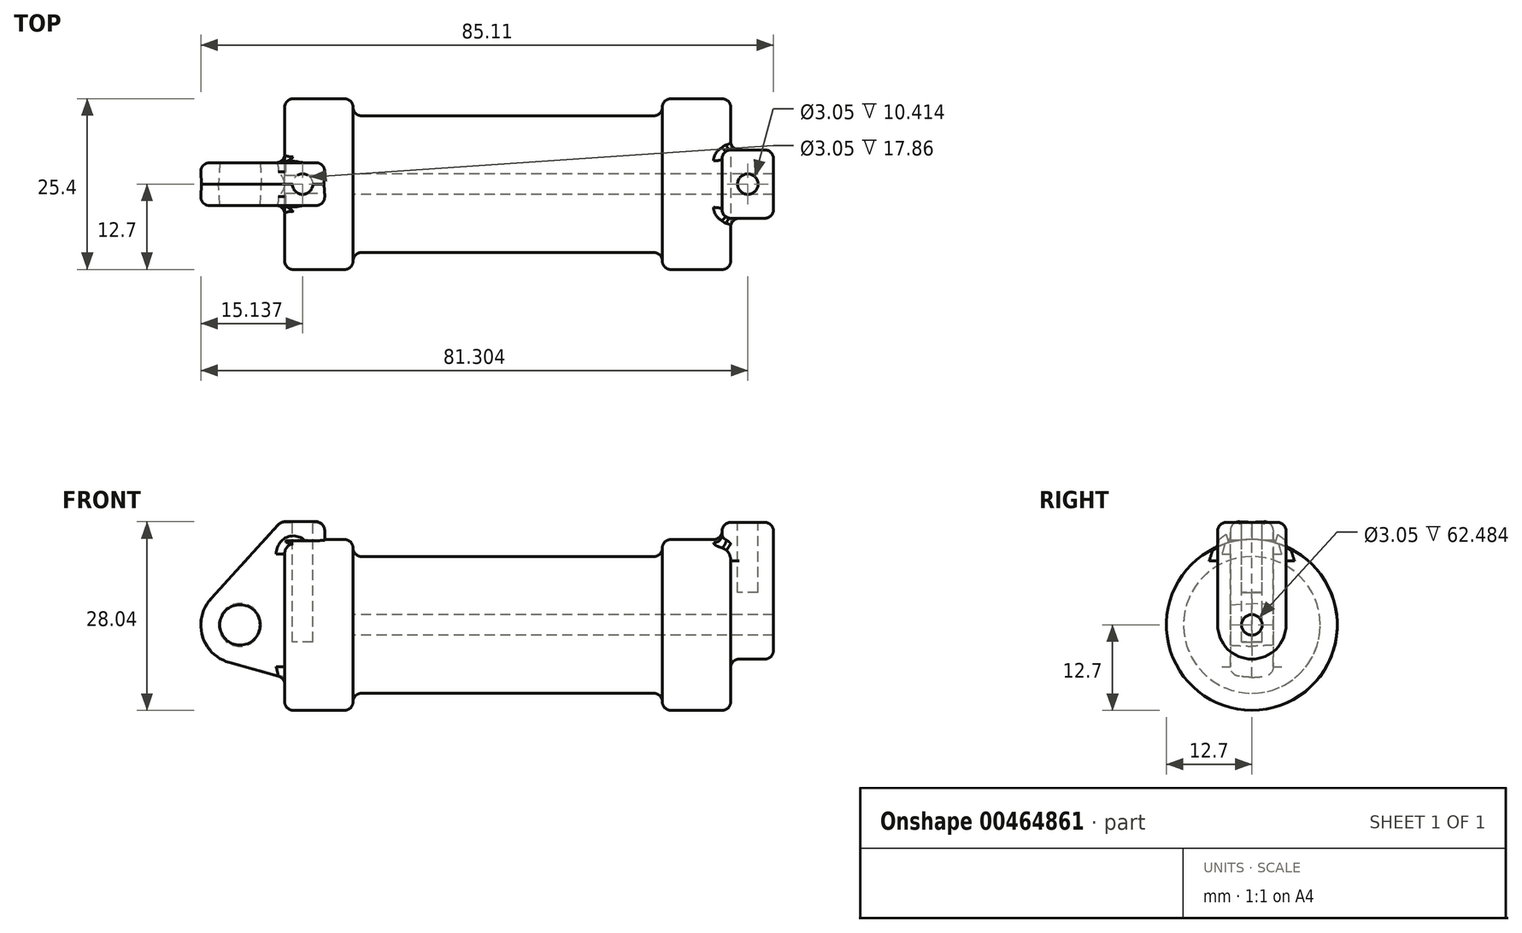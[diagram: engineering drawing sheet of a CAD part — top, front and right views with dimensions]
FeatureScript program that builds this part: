
annotation { "Feature Type Name" : "Feature", "Feature Type Description" : "" }
export const myFeature = defineFeature(function(context is Context, id is Id, definition is map)
    precondition{}
    {
        {
            var Q0;
            Q0=qCreatedBy(makeId("Front.planeOp"),FACE);
            var sketch = newSketch(context, id + "F0", { "sketchPlane" : qUnion([Q0])});
            skLineSegment(sketch, "E0", {"start": v(0, 0) * mm, "end": v(0, 12.7) * mm});
            skLineSegment(sketch, "E1", {"start": v(0, 12.7) * mm, "end": v(10.16, 12.7) * mm});
            skLineSegment(sketch, "E2", {"start": v(10.16, 12.7) * mm, "end": v(10.16, 10.16) * mm});
            skLineSegment(sketch, "E3", {"start": v(10.16, 10.16) * mm, "end": v(56.13, 10.16) * mm});
            skLineSegment(sketch, "E4", {"start": v(56.13, 10.16) * mm, "end": v(56.13, 12.7) * mm});
            skLineSegment(sketch, "E5", {"start": v(56.13, 12.7) * mm, "end": v(66.3, 12.7) * mm});
            skLineSegment(sketch, "E6", {"start": v(66.3, 12.7) * mm, "end": v(66.3, 0) * mm});
            skLineSegment(sketch, "E7", {"start": v(66.3, 0) * mm, "end": v(0, 0) * mm});
            skLineSegment(sketch, "E8", {"start": v(5.84, 15.24) * mm, "end": v(-0.5, 15.24) * mm});
            skLineSegment(sketch, "E9", {"start": v(-0.5, 15.24) * mm, "end": v(-10.88, 3.85) * mm});
            skLineSegment(sketch, "E10", {"start": v(0, 0) * mm, "end": v(-6.65, 0) * mm});
            skCircle(sketch, "E11", {"center": v(-6.65, 0) * mm, "radius": 5.72 * mm});
            skCircle(sketch, "E12", {"center": v(-6.65, 0) * mm, "radius": 3.18 * mm});
            skLineSegment(sketch, "E13", {"start": v(5.84, 15.24) * mm, "end": v(5.84, -9.4) * mm});
            skLineSegment(sketch, "E14", {"start": v(5.84, -9.4) * mm, "end": v(-8.18, -5.5) * mm});
            skLineSegment(sketch, "E15", {"start": v(0, 0) * mm, "end": v(0, -7.78) * mm});
            skSolve(sketch);
        }
        {
            var Q0;
            {var subQ0=sQuery(id+"F0.wireOp",EDGE,"E2");Q0=makeQuery(id+"F0.imprint","IMPRINT",FACE,{"disambiguationData":[TD([[makeQuery(id+"F0.imprint","IMPRINT",EDGE,{"derivedFrom":subQ0}),-1.0]])]});}
            var Q1;
            {var subQ0=sQuery(id+"F0.wireOp",EDGE,"E0");Q1=makeQuery(id+"F0.imprint","IMPRINT",FACE,{"disambiguationData":[TD([[makeQuery(id+"F0.imprint","IMPRINT",EDGE,{"derivedFrom":subQ0}),-1.0]])]});}
            var Q2;
            Q2=sQuery(id+"F0.wireOp",EDGE,"E7");
            revolve(context, id + "F1", {"entities" : qUnion([Q0, Q1]), "axis" : qUnion([Q2]), "revolveType" : RevolveType.FULL});
        }
        {
            var Q0;
            {var subQ1=sQuery(id+"F0.wireOp",EDGE,"E0");Q0=makeQuery(id+"F0.imprint","IMPRINT",FACE,{"disambiguationData":[TD([[makeQuery(id+"F0.imprint","IMPRINT",EDGE,{"derivedFrom":subQ1}),1.0]])]});}
            var Q1;
            {var subQ5=sQuery(id+"F0.wireOp",EDGE,"E12");Q1=makeQuery(id+"F0.imprint","IMPRINT",FACE,{"disambiguationData":[TD([[makeQuery(id+"F0.imprint","IMPRINT",EDGE,{"derivedFrom":subQ5}),-1.0]])]});}
            var Q2;
            {var subQ0=sQuery(id+"F0.wireOp",EDGE,"E15");Q2=makeQuery(id+"F0.imprint","IMPRINT",FACE,{"disambiguationData":[TD([[makeQuery(id+"F0.imprint","IMPRINT",EDGE,{"derivedFrom":subQ0}),-1.0]])]});}
            extrude(context, id + "F2", {"entities" : qUnion([Q0, Q1, Q2]), "operationType" : NewBodyOperationType.ADD, "endBound" : BoundingType.SYMMETRIC, "depth" : 6.35 * mm, "hasDraft" : true, "draftAngle" : 3 * degree});
        }
        {
            var Q0;
            Q0=makeQuery(id+"F1.opRevolve","SWEPT_FACE",FACE,{"disambiguationData":[OSD([sQuery(id+"F0.wireOp",EDGE,"E6")])]});
            var sketch = newSketch(context, id + "F3", { "sketchPlane" : qUnion([Q0])});
            skCircle(sketch, "E16", {"center": v(0, 0) * mm, "radius": 1.52 * mm});
            skCircle(sketch, "E17", {"center": v(0, 0) * mm, "radius": 5.08 * mm});
            skLineSegment(sketch, "E18", {"start": v(-5.08, 0) * mm, "end": v(-5.08, 15.24) * mm});
            skLineSegment(sketch, "E19", {"start": v(-5.08, 15.24) * mm, "end": v(5.08, 15.24) * mm});
            skLineSegment(sketch, "E20", {"start": v(5.08, 15.24) * mm, "end": v(5.08, 0) * mm});
            skSolve(sketch);
        }
        {
            var Q0;
            Q0 = qSketchRegion(id + "F3", true);
            extrude(context, id + "F4", {"entities" : qUnion([Q0]), "operationType" : NewBodyOperationType.ADD, "depth" : 6.35 * mm});
        }
        {
            var Q0;
            Q0 = qSketchRegion(id + "F3", true);
            extrude(context, id + "F5", {"entities" : qUnion([Q0]), "operationType" : NewBodyOperationType.ADD, "oppositeDirection" : true, "depth" : 1.27 * mm});
        }
        {
            var Q0;
            Q0=makeQuery(id+"F4.boolean.opBoolean","SPLIT",FACE,{"disambiguationData":[TD([makeQuery(id+"F4.opExtrude","SWEPT_FACE",FACE,{"disambiguationData":[OSD([sQuery(id+"F3.wireOp",EDGE,"E16")])]})])],"derivedFrom":makeQuery(id+"F1.opRevolve","SWEPT_FACE",FACE,{"disambiguationData":[OSD([sQuery(id+"F0.wireOp",EDGE,"E6")])]})});
            var Q1;
            Q1=makeQuery(id+"F1.opRevolve","SWEPT_FACE",FACE,{"disambiguationData":[OSD([sQuery(id+"F0.wireOp",EDGE,"E2")])]});
            extrude(context, id + "F6", {"entities" : qUnion([Q0]), "operationType" : NewBodyOperationType.REMOVE, "endBound" : BoundingType.UP_TO_SURFACE, "oppositeDirection" : true, "endBoundEntityFace" : qUnion([Q1]), "depth" : 25.4 * mm});
        }
        {
            var Q0;
            {var subQ0=sQuery(id+"F3.wireOp",EDGE,"E19");Q0=makeQuery(id+"F5.boolean.opBoolean","MERGE",FACE,{"derivedFrom":[makeQuery(id+"F4.opExtrude","SWEPT_FACE",FACE,{"disambiguationData":[OSD([subQ0])]}),makeQuery(id+"F5.opExtrude","SWEPT_FACE",FACE,{"disambiguationData":[OSD([subQ0])]})]});}
            var sketch = newSketch(context, id + "F7", { "sketchPlane" : qUnion([Q0])});
            skCircle(sketch, "E21", {"center": v(68.83, 0) * mm, "radius": 1.52 * mm});
            skPoint(sketch, "E22.endSnap0", {"position": v(65.02, 0) * mm});
            skSolve(sketch);
        }
        {
            var Q0;
            Q0 = qSketchRegion(id + "F7", true);
            extrude(context, id + "F8", {"entities" : qUnion([Q0]), "operationType" : NewBodyOperationType.REMOVE, "oppositeDirection" : true, "depth" : 10.4 * mm});
        }
        {
            var Q0;
            {var subQ0=sQuery(id+"F3.wireOp",EDGE,"E19");Q0=makeQuery(id+"F5.boolean.opBoolean","MERGE",FACE,{"derivedFrom":[makeQuery(id+"F4.opExtrude","SWEPT_FACE",FACE,{"disambiguationData":[OSD([subQ0])]}),makeQuery(id+"F5.opExtrude","SWEPT_FACE",FACE,{"disambiguationData":[OSD([subQ0])]})]});}
            var sketch = newSketch(context, id + "F9", { "sketchPlane" : qUnion([Q0])});
            skLineSegment(sketch, "E23.0", {"start": v(5.84, 0) * mm, "end": v(-0.5, 0) * mm});
            skCircle(sketch, "E24", {"center": v(2.67, 0) * mm, "radius": 1.52 * mm});
            skSolve(sketch);
        }
        {
            var Q0;
            Q0 = qSketchRegion(id + "F9", true);
            extrude(context, id + "F10", {"entities" : qUnion([Q0]), "operationType" : NewBodyOperationType.REMOVE, "oppositeDirection" : true, "depth" : 17.78 * mm, "hasSecondDirection" : true, "secondDirectionOppositeDirection" : false, "secondDirectionDepth" : 25.4 * mm});
        }
        {
            var Q0;
            Q0=makeQuery(id+"F1.opRevolve","SWEPT_EDGE",EDGE,{"disambiguationData":[OSD([sQuery(id+"F0.wireOp",EDGE,"E0"),sQuery(id+"F0.wireOp",EDGE,"E1")])]});
            var Q1;
            Q1=makeQuery(id+"F1.opRevolve","SWEPT_EDGE",EDGE,{"disambiguationData":[OSD([sQuery(id+"F0.wireOp",EDGE,"E1"),sQuery(id+"F0.wireOp",EDGE,"E2")])]});
            var Q2;
            Q2=makeQuery(id+"F1.opRevolve","SWEPT_EDGE",EDGE,{"disambiguationData":[OSD([sQuery(id+"F0.wireOp",EDGE,"E2"),sQuery(id+"F0.wireOp",EDGE,"E3")])]});
            var Q3;
            Q3=makeQuery(id+"F1.opRevolve","SWEPT_EDGE",EDGE,{"disambiguationData":[OSD([sQuery(id+"F0.wireOp",EDGE,"E4"),sQuery(id+"F0.wireOp",EDGE,"E5")])]});
            var Q4;
            Q4=makeQuery(id+"F1.opRevolve","SWEPT_EDGE",EDGE,{"disambiguationData":[OSD([sQuery(id+"F0.wireOp",EDGE,"E3"),sQuery(id+"F0.wireOp",EDGE,"E4")])]});
            var Q5;
            {var subQ0=sQuery(id+"F0.wireOp",EDGE,"E5");var subQ1=sQuery(id+"F0.wireOp",EDGE,"E6");Q5=makeQuery(id+"F4.boolean.opBoolean","SPLIT",EDGE,{"disambiguationData":[topologyDisambiguationEdgeConnected([makeQuery(id+"F1.opRevolve","SWEPT_FACE",FACE,{"disambiguationData":[OSD([subQ1])]})])],"derivedFrom":makeQuery(id+"F1.opRevolve","SWEPT_EDGE",EDGE,{"disambiguationData":[OSD([subQ0,subQ1])]})});}
            fillet(context, id + "F11", {"entities" : qUnion([Q0, Q1, Q2, Q3, Q4, Q5]), "radius" : 1.27 * mm, "tangentPropagation" : true, "allowEdgeOverflow" : false});
        }
        {
            var Q0;
            Q0=makeQuery(id+"F4.opExtrude","CAP_EDGE",EDGE,{"disambiguationData":[OSD([sQuery(id+"F3.wireOp",EDGE,"E19")])],"isStart":false});
            var Q1;
            Q1=makeQuery(id+"F4.opExtrude","CAP_EDGE",EDGE,{"disambiguationData":[OSD([sQuery(id+"F3.wireOp",EDGE,"E18")])],"isStart":false});
            var Q2;
            Q2=makeQuery(id+"F4.opExtrude","CAP_EDGE",EDGE,{"disambiguationData":[OSD([sQuery(id+"F3.wireOp",EDGE,"E17")])],"isStart":false});
            var Q3;
            Q3=makeQuery(id+"F4.opExtrude","CAP_EDGE",EDGE,{"disambiguationData":[OSD([sQuery(id+"F3.wireOp",EDGE,"E20")])],"isStart":false});
            var Q4;
            {var subQ0=sQuery(id+"F3.wireOp",EDGE,"E20");var subQ1=sQuery(id+"F3.wireOp",EDGE,"E19");Q4=makeQuery(id+"F5.boolean.opBoolean","MERGE",EDGE,{"derivedFrom":[makeQuery(id+"F4.opExtrude","SWEPT_EDGE",EDGE,{"disambiguationData":[OSD([subQ1,subQ0])]}),makeQuery(id+"F5.opExtrude","SWEPT_EDGE",EDGE,{"disambiguationData":[OSD([subQ1,subQ0])]})]});}
            var Q5;
            {var subQ0=sQuery(id+"F3.wireOp",EDGE,"E19");var subQ1=sQuery(id+"F3.wireOp",EDGE,"E18");Q5=makeQuery(id+"F5.boolean.opBoolean","MERGE",EDGE,{"derivedFrom":[makeQuery(id+"F4.opExtrude","SWEPT_EDGE",EDGE,{"disambiguationData":[OSD([subQ1,subQ0])]}),makeQuery(id+"F5.opExtrude","SWEPT_EDGE",EDGE,{"disambiguationData":[OSD([subQ1,subQ0])]})]});}
            var Q6;
            Q6=makeQuery(id+"F5.opExtrude","CAP_EDGE",EDGE,{"disambiguationData":[OSD([sQuery(id+"F3.wireOp",EDGE,"E19")])],"isStart":false});
            var Q7;
            Q7=makeQuery(id+"F5.boolean.opBoolean","INTERSECT",EDGE,{"derivedFrom":[makeQuery(id+"F1.opRevolve","SWEPT_FACE",FACE,{"disambiguationData":[OSD([sQuery(id+"F0.wireOp",EDGE,"E5")])]}),makeQuery(id+"F5.opExtrude","CAP_FACE",FACE,{"disambiguationData":[OSD([sQuery(id+"F3.wireOp",EDGE,"E16"),sQuery(id+"F3.wireOp",EDGE,"E17"),sQuery(id+"F3.wireOp",EDGE,"E18"),sQuery(id+"F3.wireOp",EDGE,"E19"),sQuery(id+"F3.wireOp",EDGE,"E20")])],"isStart":false})]});
            var Q8;
            Q8=makeQuery(id+"F5.opExtrude","CAP_EDGE",EDGE,{"disambiguationData":[OSD([sQuery(id+"F3.wireOp",EDGE,"E20")])],"isStart":false});
            var Q9;
            {var subQ0=sQuery(id+"F3.wireOp",EDGE,"E20");var subQ1=sQuery(id+"F0.wireOp",EDGE,"E5");var subQ2=sQuery(id+"F0.wireOp",EDGE,"E6");Q9=makeQuery(id+"F11.opFillet","BLEND_EDGE",EDGE,{"blendedFrom":[makeQuery(id+"F4.boolean.opBoolean","SPLIT",EDGE,{"disambiguationData":[topologyDisambiguationEdgeConnected([makeQuery(id+"F1.opRevolve","SWEPT_FACE",FACE,{"disambiguationData":[OSD([subQ2])]})])],"derivedFrom":makeQuery(id+"F1.opRevolve","SWEPT_EDGE",EDGE,{"disambiguationData":[OSD([subQ1,subQ2])]})}),makeQuery(id+"F5.boolean.opBoolean","MERGE",FACE,{"derivedFrom":[makeQuery(id+"F4.opExtrude","SWEPT_FACE",FACE,{"disambiguationData":[OSD([subQ0])]}),makeQuery(id+"F5.opExtrude","SWEPT_FACE",FACE,{"disambiguationData":[OSD([subQ0])]})]})],"blendedInto":[makeQuery(id+"F5.boolean.opBoolean","MERGE",FACE,{"derivedFrom":[makeQuery(id+"F4.opExtrude","SWEPT_FACE",FACE,{"disambiguationData":[OSD([subQ0])]}),makeQuery(id+"F5.opExtrude","SWEPT_FACE",FACE,{"disambiguationData":[OSD([subQ0])]})]})]});}
            var Q10;
            Q10=makeQuery(id+"F5.opExtrude","CAP_EDGE",EDGE,{"disambiguationData":[OSD([sQuery(id+"F3.wireOp",EDGE,"E18")])],"isStart":false});
            fillet(context, id + "F12", {"entities" : qUnion([Q0, Q1, Q2, Q3, Q4, Q5, Q6, Q7, Q8, Q9, Q10]), "radius" : 1.27 * mm, "tangentPropagation" : true, "allowEdgeOverflow" : false});
        }
        {
            var Q0;
            {var subQ0=sQuery(id+"F0.wireOp",EDGE,"E0");Q0=makeQuery(id+"F2.boolean.opBoolean","INTERSECT",EDGE,{"derivedFrom":[makeQuery(id+"F1.opRevolve","SWEPT_FACE",FACE,{"disambiguationData":[OSD([subQ0])]}),makeQuery(id+"F2.opExtrude","CAP_FACE",FACE,{"disambiguationData":[OSD([subQ0,sQuery(id+"F0.wireOp",EDGE,"E1"),sQuery(id+"F0.wireOp",EDGE,"E8"),sQuery(id+"F0.wireOp",EDGE,"E9"),sQuery(id+"F0.wireOp",EDGE,"E11"),sQuery(id+"F0.wireOp",EDGE,"E12"),sQuery(id+"F0.wireOp",EDGE,"E13"),sQuery(id+"F0.wireOp",EDGE,"E14"),sQuery(id+"F0.wireOp",EDGE,"E15")])],"isStart":false})]});}
            var Q1;
            Q1=makeQuery(id+"F2.opExtrude","CAP_EDGE",EDGE,{"disambiguationData":[OSD([sQuery(id+"F0.wireOp",EDGE,"E14")])],"isStart":false});
            var Q2;
            Q2=makeQuery(id+"F2.opExtrude","CAP_EDGE",EDGE,{"disambiguationData":[OSD([sQuery(id+"F0.wireOp",EDGE,"E14")])],"isStart":true});
            var Q3;
            {var subQ0=sQuery(id+"F0.wireOp",EDGE,"E0");Q3=makeQuery(id+"F2.boolean.opBoolean","INTERSECT",EDGE,{"derivedFrom":[makeQuery(id+"F1.opRevolve","SWEPT_FACE",FACE,{"disambiguationData":[OSD([subQ0])]}),makeQuery(id+"F2.opExtrude","CAP_FACE",FACE,{"disambiguationData":[OSD([subQ0,sQuery(id+"F0.wireOp",EDGE,"E1"),sQuery(id+"F0.wireOp",EDGE,"E8"),sQuery(id+"F0.wireOp",EDGE,"E9"),sQuery(id+"F0.wireOp",EDGE,"E11"),sQuery(id+"F0.wireOp",EDGE,"E12"),sQuery(id+"F0.wireOp",EDGE,"E13"),sQuery(id+"F0.wireOp",EDGE,"E14"),sQuery(id+"F0.wireOp",EDGE,"E15")])],"isStart":true})]});}
            var Q4;
            Q4=makeQuery(id+"F2.*.split.splitOp","SPLIT",EDGE,{"derivedFrom":makeQuery(id+"F2.opExtrude","SWEPT_EDGE",EDGE,{"disambiguationData":[OSD([sQuery(id+"F0.wireOp",EDGE,"E8"),sQuery(id+"F0.wireOp",EDGE,"E9")])]})});
            var Q5;
            Q5=makeQuery(id+"F2.*.split.splitOp","SPLIT",EDGE,{"derivedFrom":makeQuery(id+"F2.opExtrude","SWEPT_EDGE",EDGE,{"disambiguationData":[OSD([sQuery(id+"F0.wireOp",EDGE,"E8"),sQuery(id+"F0.wireOp",EDGE,"E9")])]}),"isFromBackBody":true});
            var Q6;
            Q6=makeQuery(id+"F2.opExtrude","CAP_EDGE",EDGE,{"disambiguationData":[OSD([sQuery(id+"F0.wireOp",EDGE,"E8")])],"isStart":true});
            var Q7;
            Q7=makeQuery(id+"F2.opExtrude","CAP_EDGE",EDGE,{"disambiguationData":[OSD([sQuery(id+"F0.wireOp",EDGE,"E8")])],"isStart":false});
            var Q8;
            Q8=makeQuery(id+"F2.opExtrude","CAP_EDGE",EDGE,{"disambiguationData":[OSD([sQuery(id+"F0.wireOp",EDGE,"E13")])],"isStart":false});
            var Q9;
            Q9=makeQuery(id+"F2.opExtrude","CAP_EDGE",EDGE,{"disambiguationData":[OSD([sQuery(id+"F0.wireOp",EDGE,"E13")])],"isStart":true});
            var Q10;
            Q10=makeQuery(id+"F2.*.split.splitOp","SPLIT",EDGE,{"derivedFrom":makeQuery(id+"F2.opExtrude","SWEPT_EDGE",EDGE,{"disambiguationData":[OSD([sQuery(id+"F0.wireOp",EDGE,"E8"),sQuery(id+"F0.wireOp",EDGE,"E13")])]}),"isFromBackBody":true});
            var Q11;
            Q11=makeQuery(id+"F2.*.split.splitOp","SPLIT",EDGE,{"derivedFrom":makeQuery(id+"F2.opExtrude","SWEPT_EDGE",EDGE,{"disambiguationData":[OSD([sQuery(id+"F0.wireOp",EDGE,"E8"),sQuery(id+"F0.wireOp",EDGE,"E13")])]})});
            fillet(context, id + "F13", {"entities" : qUnion([Q0, Q1, Q2, Q3, Q4, Q5, Q6, Q7, Q8, Q9, Q10, Q11]), "radius" : 1.27 * mm, "tangentPropagation" : true, "allowEdgeOverflow" : false});
        }
    });
